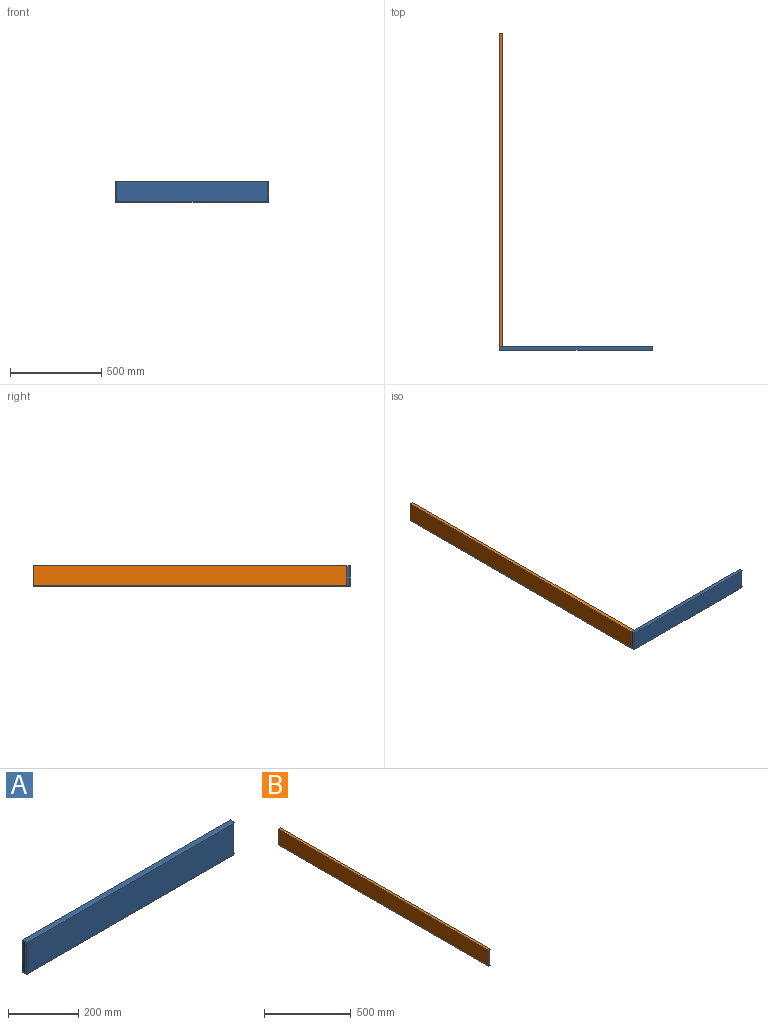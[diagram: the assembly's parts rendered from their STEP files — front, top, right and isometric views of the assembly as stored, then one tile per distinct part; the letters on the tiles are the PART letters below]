
ASSEMBLY  parts=2 mates=1
PART A: 14 faces, bbox 838.2x19.1x114.3 mm
  f0: plane 825.5x6.35mm, normal (0,0,-1), area 5241.9mm2, adj f9,f10,f12,f13
  f1: plane 838.2x107.95mm, normal (0,1,0), area 90483.7mm2, adj f2,f4,f5,f12
  f2: plane 107.95x12.7mm, normal (1,0,0), area 1371mm2, adj f1,f5,f6,f10
  f3: plane 825.5x107.95mm, normal (0,-1,0), area 89112.7mm2, adj f5,f6,f8,f9
  f4: plane 107.95x12.7mm, normal (-1,0,0), area 1371mm2, adj f1,f5,f8,f13
  f5: plane 838.2x19.05mm, normal (0,0,1), area 15950.4mm2, adj f1,f2,f3,f4,f6,f8
  f6: cylinder r=6.35mm len=107.95mm, axis (0,0,1), area 1076.8mm2, adj f2,f3,f5,f7
  f7: sphere r=6.35mm, area 63.3mm2, adj f6,f9,f10
  f8: cylinder r=6.35mm len=107.95mm, axis (0,0,1), area 1076.8mm2, adj f3,f4,f5,f11
  f9: cylinder r=6.35mm len=825.5mm, axis (1,0,0), area 8234mm2, adj f0,f3,f7,f11
  f10: cylinder r=6.35mm len=12.7mm, axis (0,1,0), area 103.7mm2, adj f0,f2,f7,f12
  f11: sphere r=6.35mm, area 63.3mm2, adj f8,f9,f13
  f12: cylinder r=6.35mm len=838.2mm, axis (-1,0,0), area 8314.6mm2, adj f0,f1,f10,f13
  f13: cylinder r=6.35mm len=12.7mm, axis (0,-1,0), area 103.7mm2, adj f0,f4,f11,f12
PART B: 8 faces, bbox 19.1x1714.5x114.3 mm
  f0: plane 114.3x12.7mm, normal (0,-1,0), area 1443mm2, adj f1,f4,f5,f6,f7
  f1: plane 1714.5x107.95mm, normal (-1,0,0), area 185080.3mm2, adj f0,f2,f5,f7
  f2: plane 114.3x19.05mm, normal (0,1,0), area 2168.8mm2, adj f1,f3,f4,f5,f7
  f3: plane 1708.15x114.3mm, normal (1,0,0), area 195241.5mm2, adj f2,f4,f5,f6
  f4: plane 1714.5x12.7mm, normal (0,0,-1), area 21765.5mm2, adj f0,f2,f3,f6,f7
  f5: plane 1714.5x19.05mm, normal (0,0,1), area 32652.6mm2, adj f0,f1,f2,f3,f6
  f6: cylinder r=6.35mm len=114.3mm, axis (0,0,-1), area 1140.1mm2, adj f0,f3,f4,f5
  f7: cylinder r=6.35mm len=1714.5mm, axis (0,-1,0), area 17101.4mm2, adj f0,f1,f2,f4
PLACE A at identity
PLACE B at identity
MATE fastened B.f5 <-> A.f5  axis (0,0,1) through (2328.86,-1543.05,180.98)mm
